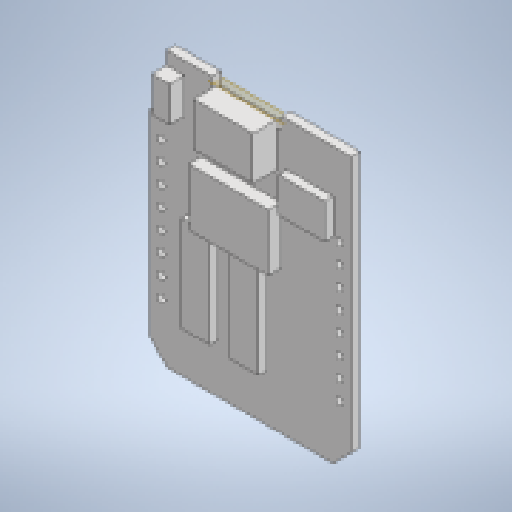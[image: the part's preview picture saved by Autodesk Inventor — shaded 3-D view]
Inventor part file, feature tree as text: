
AUTODESK INVENTOR PART (.ipt)
format: ipt  version: 2023 (Build 270158000, 158)  size: 365,568 bytes
history: native  units: mm
features: extrude x8, sketch x6, plane x1, projected_geometry x1
ambient origin geometry x8: Origin, YZ Plane, XZ Plane, XY Plane, X Axis, Y Axis, Z Axis, Center Point
bodies: Body1 (feature_tree)
feature tree (16):
  extrude  "Extrusion2"  Depth=35.0mm
  plane  "Work Plane1"
  extrude  "Extrusion3"  Depth=7.65mm
  extrude  "Extrusion4"  Depth=8.88mm
  extrude  "Extrusion5"  Depth=1.0mm
  sketch  "Sketch5"  dims[d11=1.5mm d12=7.3mm]
  extrude  "Extrusion6"  Depth=7.3mm
  extrude  "Extrusion7"  Depth=2.3mm
  extrude  "Extrusion8"  Depth=2.3mm
  extrude  "Extrusion9"  Depth=1.13mm TaperAngle=0.0deg
  sketch  "Sketch1"  dims[d0=25.7mm d1=35.0mm]
  sketch  "Sketch2"  dims[d4=2.18mm d5=7.65mm]
  projected_geometry  "Projected Loop1"
  sketch  "Sketch3"  dims[d7=5.8mm d8=8.88mm]
  sketch  "Sketch4"  dims[d9=1.6mm d10=1.0mm]
  sketch  "Sketch6"  dims[d13=80.0mm d15=2.5mm d16=10.0mm d18=10.0mm d20=2.3mm d21=2.3mm d22=1.13mm d23=0.0mm d24=0.9mm d25=7.57mm d26=3.0mm d27=0.0mm d28=0.0mm d29=5.5mm d30=0.0mm d31=10.55mm d32=16.0mm d33=5.1mm d34=0.5mm d35=1.0mm d36=0.0mm d37=12.0mm d38=15.1mm d39=7.8mm d40=2.0mm d41=2.3mm d42=0.0mm d43=1.7mm d44=2.25mm d45=4.5mm d46=6.31mm d47=3.6mm d48=5.2mm d49=12.2mm d50=6.64mm d51=7.29mm d52=18.66mm d53=6.56mm d54=11.66mm d55=3.7mm d56=15.0mm d57=10.1mm d58=1.85mm d59=0.0mm d60=1.1mm d61=0.0mm d62=1.6mm d63=0.0mm d64=3.0mm d65=5.76mm d66=1.7mm d67=0.5mm d68=0.65mm d69=0.0mm]
